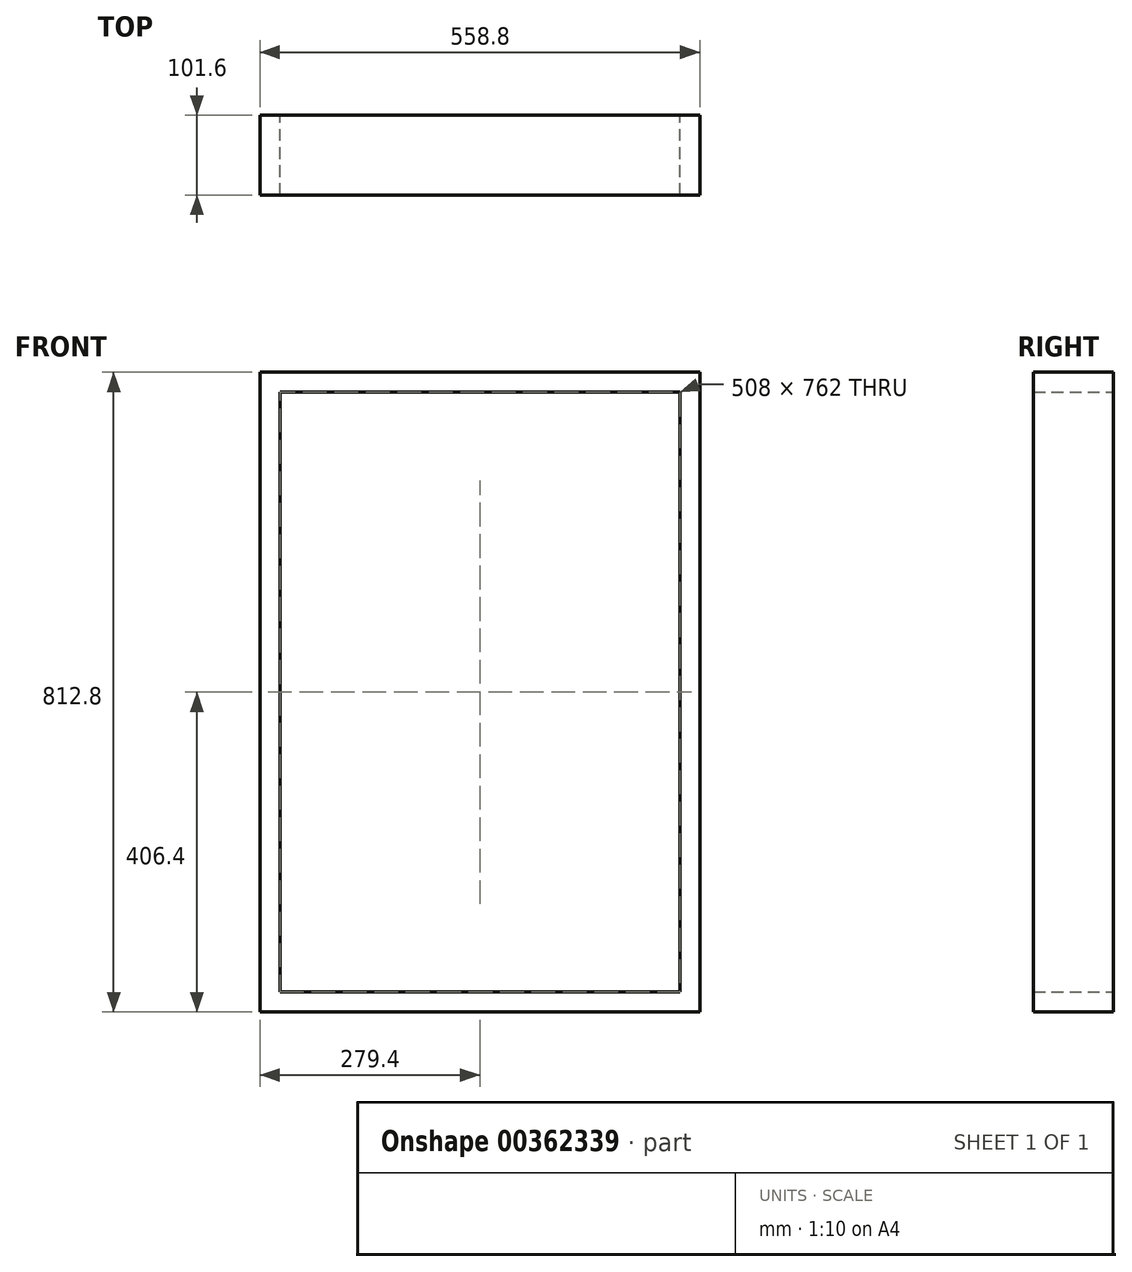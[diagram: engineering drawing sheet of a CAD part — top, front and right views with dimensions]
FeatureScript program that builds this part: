
annotation { "Feature Type Name" : "Feature", "Feature Type Description" : "" }
export const myFeature = defineFeature(function(context is Context, id is Id, definition is map)
    precondition{}
    {
        {
            var Q0;
            Q0=qCreatedBy(makeId("Front.planeOp"),FACE);
            var sketch = newSketch(context, id + "F0", { "sketchPlane" : qUnion([Q0])});
            skLineSegment(sketch, "E0.bottom", {"start": v(279.4, 406.4) * mm, "end": v(-279.4, 406.4) * mm});
            skLineSegment(sketch, "E0.top", {"start": v(279.4, -406.4) * mm, "end": v(-279.4, -406.4) * mm});
            skLineSegment(sketch, "E0.left", {"start": v(279.4, 406.4) * mm, "end": v(279.4, -406.4) * mm});
            skLineSegment(sketch, "E0.right", {"start": v(-279.4, 406.4) * mm, "end": v(-279.4, -406.4) * mm});
            skPoint(sketch, "E0.middle", {"position": v(0, 0) * mm});
            skLineSegment(sketch, "E1.0", {"start": v(254, 381) * mm, "end": v(-254, 381) * mm});
            skLineSegment(sketch, "E1.1", {"start": v(254, 381) * mm, "end": v(254, -381) * mm});
            skLineSegment(sketch, "E1.2", {"start": v(254, -381) * mm, "end": v(-254, -381) * mm});
            skLineSegment(sketch, "E1.3", {"start": v(-254, 381) * mm, "end": v(-254, -381) * mm});
            skSolve(sketch);
        }
        {
            var Q0;
            Q0=makeQuery(id+"F0.imprint","IMPRINT",FACE,{"disambiguationData":[TD([[makeQuery(id+"F0.imprint","IMPRINT",EDGE,{"derivedFrom":sQuery(id+"F0.wireOp",EDGE,"E0.bottom")}),1.0]])]});
            extrude(context, id + "F1", {"entities" : qUnion([Q0]), "depth" : 101.6 * mm});
        }
    });
